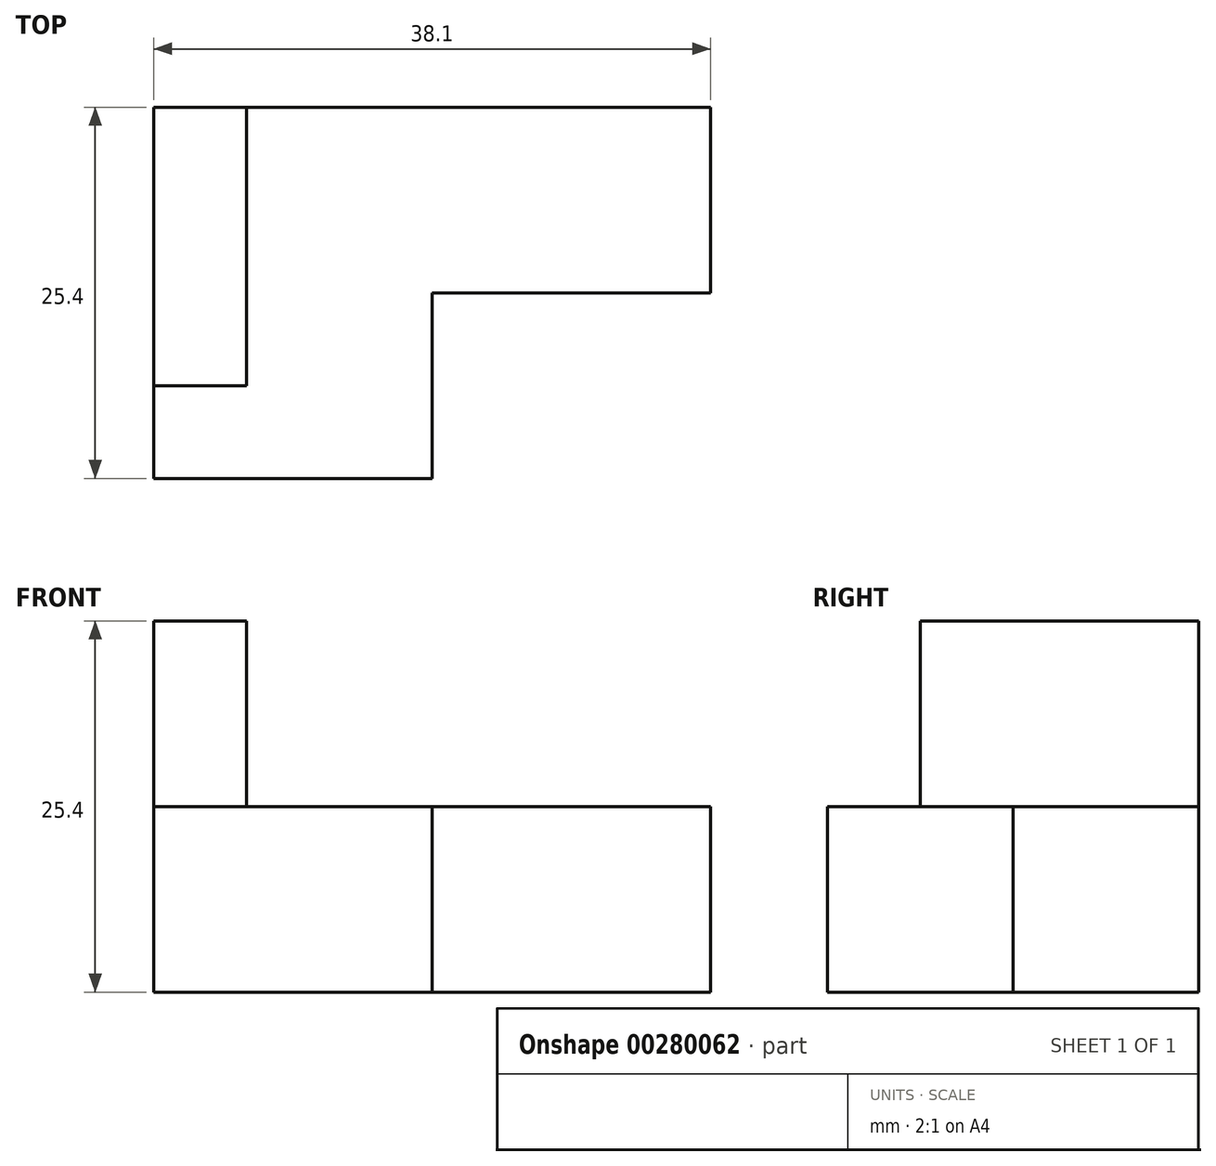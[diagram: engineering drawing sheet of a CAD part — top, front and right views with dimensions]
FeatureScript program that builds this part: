
annotation { "Feature Type Name" : "Feature", "Feature Type Description" : "" }
export const myFeature = defineFeature(function(context is Context, id is Id, definition is map)
    precondition{}
    {
        {
            var Q0;
            Q0=qCreatedBy(makeId("Top.planeOp"),FACE);
            var sketch = newSketch(context, id + "F0", { "sketchPlane" : qUnion([Q0])});
            skLineSegment(sketch, "E0.bottom", {"start": v(0, 0) * mm, "end": v(38.1, 0) * mm});
            skLineSegment(sketch, "E0.top", {"start": v(0, 25.4) * mm, "end": v(38.1, 25.4) * mm});
            skLineSegment(sketch, "E0.left", {"start": v(0, 0) * mm, "end": v(0, 25.4) * mm});
            skLineSegment(sketch, "E0.right", {"start": v(38.1, 0) * mm, "end": v(38.1, 25.4) * mm});
            skSolve(sketch);
        }
        {
            var Q0;
            Q0=makeQuery(id+"F0.imprint","IMPRINT",FACE,{"disambiguationData":[TD([[makeQuery(id+"F0.imprint","IMPRINT",EDGE,{"derivedFrom":sQuery(id+"F0.wireOp",EDGE,"E0.bottom")}),1.0]])]});
            var Q1;
            Q1=makeQuery(id+"F0.imprint","IMPRINT",FACE,{"disambiguationData":[TD([[makeQuery(id+"F0.imprint","IMPRINT",EDGE,{"derivedFrom":sQuery(id+"F0.wireOp",EDGE,"phQm5TJ8-ujtP-aQUd-Vbjd-HNTeA9L2L1z2.bottom")}),-1.0]])]});
            extrude(context, id + "F1", {"entities" : qUnion([Q0, Q1]), "depth" : 12.7 * mm});
        }
        {
            var Q0;
            Q0=makeQuery(id+"F1.opExtrude","CAP_FACE",FACE,{"disambiguationData":[OSD([sQuery(id+"F0.wireOp",EDGE,"E0.bottom"),sQuery(id+"F0.wireOp",EDGE,"E0.top"),sQuery(id+"F0.wireOp",EDGE,"E0.left"),sQuery(id+"F0.wireOp",EDGE,"E0.right")])],"isStart":false});
            var sketch = newSketch(context, id + "F2", { "sketchPlane" : qUnion([Q0])});
            skLineSegment(sketch, "E1.bottom", {"start": v(0, 25.4) * mm, "end": v(6.35, 25.4) * mm});
            skLineSegment(sketch, "E1.top", {"start": v(0, 6.35) * mm, "end": v(6.35, 6.35) * mm});
            skLineSegment(sketch, "E1.left", {"start": v(0, 25.4) * mm, "end": v(0, 6.35) * mm});
            skLineSegment(sketch, "E1.right", {"start": v(6.35, 25.4) * mm, "end": v(6.35, 6.35) * mm});
            skSolve(sketch);
        }
        {
            var Q0;
            Q0 = qSketchRegion(id + "F2", true);
            extrude(context, id + "F3", {"entities" : qUnion([Q0]), "operationType" : NewBodyOperationType.ADD, "depth" : 12.7 * mm});
        }
        {
            var Q0;
            Q0=makeQuery(id+"F1.opExtrude","CAP_FACE",FACE,{"disambiguationData":[OSD([sQuery(id+"F0.wireOp",EDGE,"E0.bottom"),sQuery(id+"F0.wireOp",EDGE,"E0.top"),sQuery(id+"F0.wireOp",EDGE,"E0.left"),sQuery(id+"F0.wireOp",EDGE,"E0.right")])],"isStart":false});
            var sketch = newSketch(context, id + "F4", { "sketchPlane" : qUnion([Q0])});
            skLineSegment(sketch, "E2.bottom", {"start": v(38.1, 0) * mm, "end": v(19.05, 0) * mm});
            skLineSegment(sketch, "E2.top", {"start": v(38.1, 12.7) * mm, "end": v(19.05, 12.7) * mm});
            skLineSegment(sketch, "E2.left", {"start": v(38.1, 0) * mm, "end": v(38.1, 12.7) * mm});
            skLineSegment(sketch, "E2.right", {"start": v(19.05, 0) * mm, "end": v(19.05, 12.7) * mm});
            skSolve(sketch);
        }
        {
            var Q0;
            Q0 = qSketchRegion(id + "F4", true);
            extrude(context, id + "F5", {"entities" : qUnion([Q0]), "operationType" : NewBodyOperationType.REMOVE, "endBound" : BoundingType.THROUGH_ALL, "oppositeDirection" : true, "depth" : 25.4 * mm});
        }
    });
